# Revit family: Toilet-Floor_Mount-KOHLER-Wellcomme_Ultra-K-96054
name_source: partatom
category: Plumbing Fixtures
revit_build: Autodesk Revit 2015 (Build: 20140606_1530(x64)
units: mm (PartAtom-declared; Revit-internal decimal feet)

## types (5) — shared parameters
ADA Compliant = No
Assembly Code = D2010100
CW Connection = Yes
Cold Water Inlet = Cold Water Inlet
Date Modified = 10/11/2018
Default Elevation = 0"
Flow Rate = 25 GPM
Flush Rate = 1.6 GPF
HW Connection = No
Height = 15 1/4"
Hot Water Inlet = Hot Water Inlet
Length = 26 3/8"
Manufacturer = KOHLER Co.
MasterFormat 1995 = 15410
MasterFormat 2004 = 22.41.13
Material = Vitreous China
Pressure = 80.00 psi
Product Documentation Link = http://www.us.kohler.com
Product Name = Wellcomme Ultra
Product Page URL = http://www.us.kohler.com
Seat Included = No
URL = https://www.us.kohler.com
Vent Connection = No
Waste Connection = Yes
Waste Water Outlet = Waste Water Outlet
Width = 14 7/8"

## per-type parameters (varying)
| type | Description | Finish | Model | Type |
| 0 - White | Flushometer bowl with rear spud | Kohler-Vitreous_China-0-White | K-96054-0 | 1 |
| 96 - Biscuit | Flushometer bowl with rear spud | Kohler-Vitreous_China-96-Biscuit | K-96054-96 | 2 |
| 47 - Almond | Flushometer bowl with rear spud | Kohler-Vitreous_China-47-Almond | K-96054-47 | 3 |
| 7 - Black Black | Flushometer bowl with rear spud | Kohler-Vitreous_China-7-Black_Black | K-96054-7 | 4 |
| Antimicrobial Finish, 0 - White | Flushometer bowl with rear spud, antimicrobial finish | Kohler-Vitreous_China-0-White | K-96054-SS-0 | 5 |

## geometry (parser evidence)
native form markers: Sweep x5
no freeform markers — native parametric forms only
